# Revit family: Camera-Security-Canon-Fixed_Micro_Dome_Camera
name_source: partatom
category: Security Devices
revit_build: Autodesk Revit MEP 2012 (Build: 20110916_2132(x64)
units: mm (PartAtom-declared; Revit-internal decimal feet)

## types (2) — shared parameters
Alarm Triggers = External Device Input, Intelligent Function (Video), Intelligent Function (Volume), Timer
Angular Field of View = Horizontal: 95; Vertical: 60
Aperture = 1.6
Audio In = Φ3.5mm (Φ0.14 in.) Mini-Jack Connector (Monaural), Switch Line IN/MIC IN in the Setting Page. LINE IN x 1 (Connect to an Amplifier Microphone) or MIC IN x 1 (Connect to a Microphone w/o Amplifier)
Date Modified = September 15, 2014
Day and Night = Auto/Manual
Default Elevation = 48 "
Description = See Part Description
Equipment Abbreviation = SC
Family Version = 1.0
IPv4 Protocol = TCP/IP, UDP, HTTP, FTP, SNMP (MIB2), SMTP (Client), DHCP (Client), DNS (Client), ARP, ICMP, POP3, NTP, SMTP Authentication, RTSP, WV-HTTP (Canon Proprietary), ONVIF
Image Sensor = 1/3 Type CMOS (Primary Color Filter)
Lens Type = Varifocal
Manufacturer = Canon U.S.A., Inc.
Maximum Framerate = JPEG: 0.1 - 30 fps; H.263: 1/2/3/5/6/10/15/30 fps
Minimum Illumination = 0 lx
Model = See Part Number
Model Disclaimer = This 3D model is a simulation of a highly customizable piece of Canon equipment. For assistance in selecting the right Canon equipment for your project, please contact Canon U.S.A., Inc.
Operating Conditions = Temperature:  -10°C - +50°C (+14°F - +122°F); Humidity: 5% - 85% (Without Condensation)
Product Documentation Link = http://www.usa.canon.com
Product Page URL = http://www.usa.canon.com
Scanning System = Progressive
URL = http://www.usa.canon.com
zz Angle 2 = 0.000°
zz Angle 3 = 0.000°
zz Length 10 = 3.345 "
zz Length 101 = 3.5 "
zz Length 102 = 4.29 "
zz Length 103 = 2 "
zz Length 104 = 6.83 "
zz Length 105 = 7.352 "
zz Length 106 = 7.08 "
zz Length 107 = 1.75 "
zz Length 109 = 0.25 "
zz Length 11 = -1.75 "
zz Length 13 = 5.306 "
zz Length 14 = 0.25 "
zz Length 16 = 2.36 "
zz Length 18 = 2.6 "
zz Length 19 = 10.404 "
zz Length 2 = 4.72 "
zz Length 20 = 1.75 "
zz Length 26 = -4.103 "
zz Length 27 = 0.697 "
zz Length 29 = 4.103 "
zz Length 3 = 2.485 "
zz Length 30 = 7 "
zz Length 32 = 3.6 "
zz Length 33 = 6.743 "
zz Length 34 = 0.125 "
zz Length 35 = 0.5 "
zz Length 36 = 8.874 "
zz Length 41 = 2 "
zz Length 42 = 2.36 "
zz Length 45 = 4.72 "
zz Length 46 = 3.937 "
zz Length 47 = 6.69 "
zz Length 48 = 6 "
zz Length 49 = 0.75 "
zz Length 50 = 1.5 "
zz Length 54 = 1.75 "
zz Length 55 = 0.125 "
zz Length 57 = 1.811 "
zz Length 59 = 0.235 "
zz Length 6 = 0.248 "
zz Length 62 = 9.724 "
zz Length 64 = 8.205 "
zz Length 65 = 1.97 "
zz Length 68 = 2.57 "
zz Length 69 = 3.97 "
zz Length 7 = 4.97 "
zz Length 72 = -6.146 "
zz Length 74 = 7.2 "
zz Length 76 = 0.47 "
zz Length 78 = 1.77 "
zz Length 79 = 13 "
zz Length 8 = 7.093 "
zz Length 82 = 5.215 "
zz Length 83 = 4.72 "
zz Length 84 = 4.72 "
zz Length 86 = 0.5 "
zz Length 88 = 7.884 "
zz Length 89 = 2.756 "
zz Length 9 = 4.72 "
zz Length 90 = 2.244 "
zz Length 91 = 7.08 "
zz Length 93 = 4.88 "
zz Length 94 = 10.253 "
zz Length 95 = 5.5 "
zz Length 96 = 3.66 "
zz Length 97 = 2.244 "
zz Length 99 = -6.5 "

## per-type parameters (varying)
| type | Effective Pixels | Megapixels | Resolution | Shutter Speed | zz Integer 1 |
| 1.3 MP - Fixed | 1.3 Million Pixels | 1.3 | JPEG, H.264: 1280 x 720, 640 x 360, 320 x 180, 1280 x 960, 640 x 480, 320 x 240 | 1, 1/2, 1/4, 1/8, 1/15, 1/30, 1/60, 1/100, 1/120, 1/250, 1/500, 1/1000, 1/2000, 1/4000, 1/8000, 1/10000, 1/16000 sec. | 1 |
| 2.1 MP - Fixed | 2.1 Million Pixels | 2.1 | JPEG, H.264: 1920 x 1080, 960 x 540, 480 x 270, 1280 x 720, 640 x 360, 320 x 180, 1280 x 960, 640 x 480, 320 x 240 | 1, 1/2, 1/4, 1/8, 1/15, 1/30, 1/60, 1/100, 1/120, 1/250, 1/500, 1/1000, 1/2000, 1/4000, 1/8000, 1/16000 sec. | 2 |

## geometry (parser evidence)
native form markers: Blend x2, Sweep x7
no freeform markers — native parametric forms only
